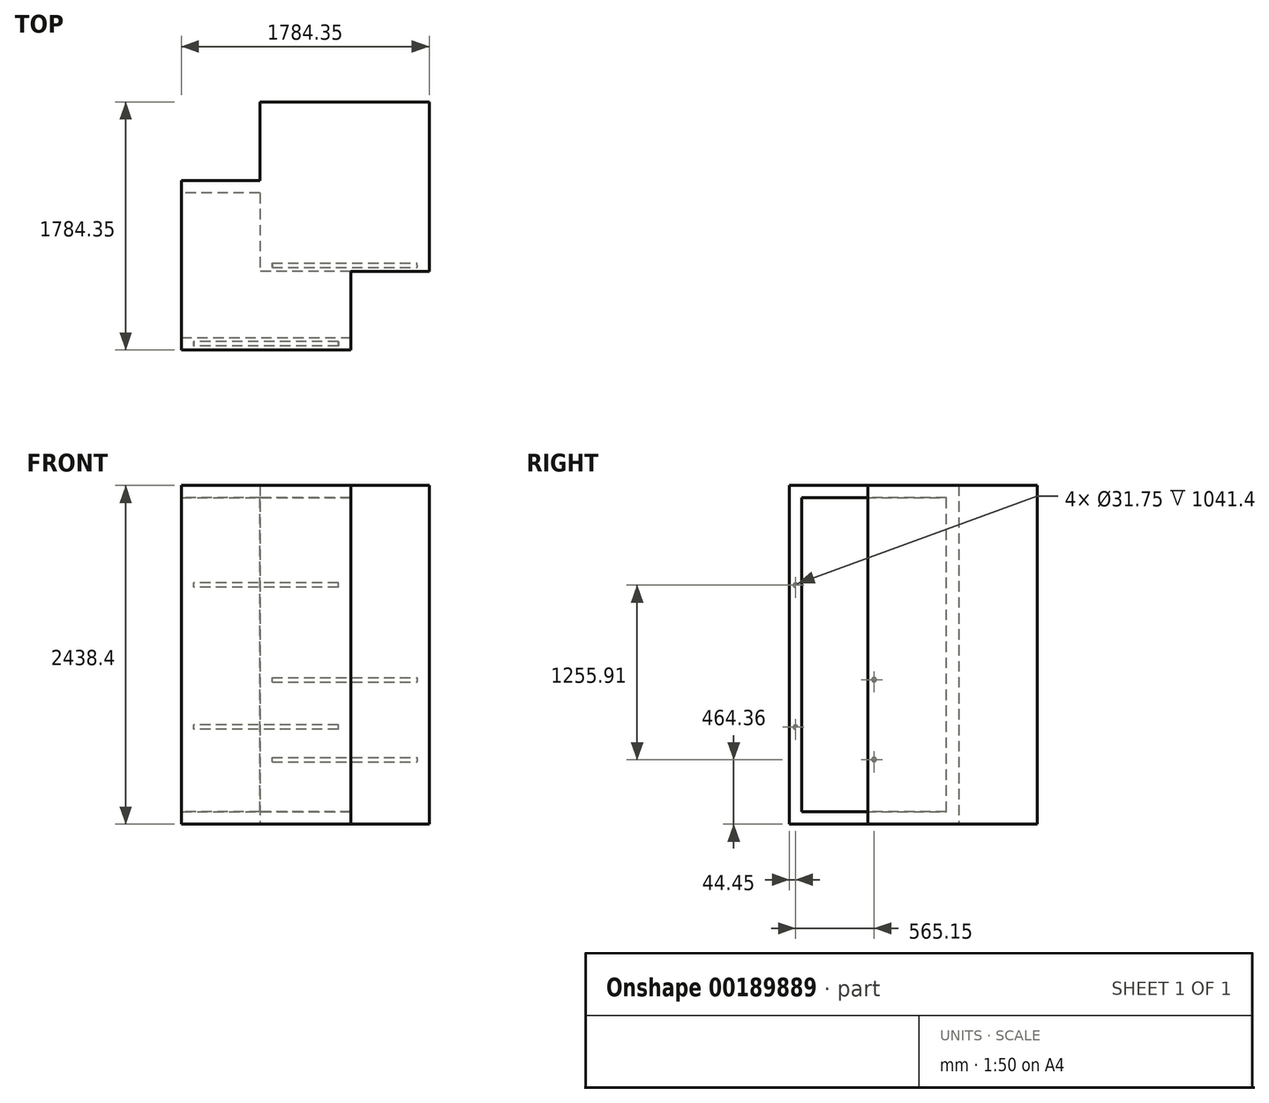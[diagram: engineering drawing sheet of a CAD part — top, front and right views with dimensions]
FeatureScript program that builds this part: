
annotation { "Feature Type Name" : "Feature", "Feature Type Description" : "" }
export const myFeature = defineFeature(function(context is Context, id is Id, definition is map)
    precondition{}
    {
        {
            var Q0;
            Q0=qCreatedBy(makeId("Top.planeOp"),FACE);
            var sketch = newSketch(context, id + "F0", { "sketchPlane" : qUnion([Q0])});
            skLineSegment(sketch, "E0.bottom", {"start": v(0, 0) * mm, "end": v(1219.2, 0) * mm});
            skLineSegment(sketch, "E0.top", {"start": v(0, 1219.2) * mm, "end": v(1219.2, 1219.2) * mm});
            skLineSegment(sketch, "E0.left", {"start": v(0, 0) * mm, "end": v(0, 1219.2) * mm});
            skLineSegment(sketch, "E0.right", {"start": v(1219.2, 0) * mm, "end": v(1219.2, 1219.2) * mm});
            skLineSegment(sketch, "E1.bottom", {"start": v(1784.35, 1784.35) * mm, "end": v(565.15, 1784.35) * mm});
            skLineSegment(sketch, "E1.top", {"start": v(1784.35, 565.15) * mm, "end": v(565.15, 565.15) * mm});
            skLineSegment(sketch, "E1.left", {"start": v(1784.35, 1784.35) * mm, "end": v(1784.35, 565.15) * mm});
            skLineSegment(sketch, "E1.right", {"start": v(565.15, 1784.35) * mm, "end": v(565.15, 565.15) * mm});
            skLineSegment(sketch, "E2.0", {"start": v(1695.45, 1695.45) * mm, "end": v(1695.45, 654.05) * mm});
            skLineSegment(sketch, "E2.1", {"start": v(1695.45, 1695.45) * mm, "end": v(654.05, 1695.45) * mm});
            skLineSegment(sketch, "E2.2", {"start": v(654.05, 1695.45) * mm, "end": v(654.05, 654.05) * mm});
            skLineSegment(sketch, "E2.3", {"start": v(1695.45, 654.05) * mm, "end": v(654.05, 654.05) * mm});
            skLineSegment(sketch, "E3.0", {"start": v(88.9, 1130.3) * mm, "end": v(1130.3, 1130.3) * mm});
            skLineSegment(sketch, "E3.1", {"start": v(88.9, 88.9) * mm, "end": v(88.9, 1130.3) * mm});
            skLineSegment(sketch, "E3.2", {"start": v(88.9, 88.9) * mm, "end": v(1130.3, 88.9) * mm});
            skLineSegment(sketch, "E3.3", {"start": v(1130.3, 88.9) * mm, "end": v(1130.3, 1130.3) * mm});
            skLineSegment(sketch, "E4", {"start": v(88.9, 765.31) * mm, "end": v(565.15, 765.31) * mm, "construction": true});
            skLineSegment(sketch, "E5", {"start": v(654.05, 765.31) * mm, "end": v(1130.3, 765.31) * mm, "construction": true});
            skLineSegment(sketch, "E6", {"start": v(800.66, 88.9) * mm, "end": v(800.66, 565.15) * mm, "construction": true});
            skLineSegment(sketch, "E7", {"start": v(800.66, 654.05) * mm, "end": v(800.66, 1130.3) * mm, "construction": true});
            skLineSegment(sketch, "E8.bottom", {"start": v(1695.45, 654.05) * mm, "end": v(1784.35, 654.05) * mm});
            skLineSegment(sketch, "E8.top", {"start": v(1695.45, 565.15) * mm, "end": v(1784.35, 565.15) * mm});
            skLineSegment(sketch, "E8.left", {"start": v(1695.45, 654.05) * mm, "end": v(1695.45, 565.15) * mm});
            skLineSegment(sketch, "E8.right", {"start": v(1784.35, 654.05) * mm, "end": v(1784.35, 565.15) * mm});
            skLineSegment(sketch, "E9.bottom", {"start": v(654.05, 654.05) * mm, "end": v(565.15, 654.05) * mm});
            skLineSegment(sketch, "E9.top", {"start": v(654.05, 565.15) * mm, "end": v(565.15, 565.15) * mm});
            skLineSegment(sketch, "E9.left", {"start": v(654.05, 654.05) * mm, "end": v(654.05, 565.15) * mm});
            skLineSegment(sketch, "E9.right", {"start": v(565.15, 654.05) * mm, "end": v(565.15, 565.15) * mm});
            skLineSegment(sketch, "E10.bottom", {"start": v(654.05, 1695.45) * mm, "end": v(565.15, 1695.45) * mm});
            skLineSegment(sketch, "E10.top", {"start": v(654.05, 1784.35) * mm, "end": v(565.15, 1784.35) * mm});
            skLineSegment(sketch, "E10.left", {"start": v(654.05, 1695.45) * mm, "end": v(654.05, 1784.35) * mm});
            skLineSegment(sketch, "E10.right", {"start": v(565.15, 1695.45) * mm, "end": v(565.15, 1784.35) * mm});
            skLineSegment(sketch, "E11.bottom", {"start": v(1695.45, 1695.45) * mm, "end": v(1784.35, 1695.45) * mm});
            skLineSegment(sketch, "E11.top", {"start": v(1695.45, 1784.35) * mm, "end": v(1784.35, 1784.35) * mm});
            skLineSegment(sketch, "E11.left", {"start": v(1695.45, 1695.45) * mm, "end": v(1695.45, 1784.35) * mm});
            skLineSegment(sketch, "E11.right", {"start": v(1784.35, 1695.45) * mm, "end": v(1784.35, 1784.35) * mm});
            skSolve(sketch);
        }
        {
            var Q0;
            {var subQ1=sQuery(id+"F0.wireOp",EDGE,"E0.right");var subQ6=sQuery(id+"F0.wireOp",EDGE,"E0.top");var subQ10=makeQuery(id+"F0.imprint","INTERSECT",VERTEX,{"derivedFrom":[subQ6,subQ1]});Q0=makeQuery(id+"F0.imprint","IMPRINT",FACE,{"disambiguationData":[TD([[makeQuery(id+"F0.imprint","IMPRINT",EDGE,{"disambiguationData":[TD([[subQ10,1.0]])],"derivedFrom":subQ6}),-1.0]])]});}
            var Q1;
            {var subQ0=sQuery(id+"F0.wireOp",EDGE,"E1.top");var subQ1=sQuery(id+"F0.wireOp",EDGE,"E0.right");var subQ2=makeQuery(id+"F0.imprint","INTERSECT",VERTEX,{"derivedFrom":[subQ1,subQ0]});Q1=makeQuery(id+"F0.imprint","IMPRINT",FACE,{"disambiguationData":[TD([[makeQuery(id+"F0.imprint","IMPRINT",EDGE,{"disambiguationData":[TD([[subQ2,-1.0]])],"derivedFrom":subQ1}),1.0]])]});}
            var Q2;
            {var subQ1=sQuery(id+"F0.wireOp",EDGE,"E0.bottom");Q2=makeQuery(id+"F0.imprint","IMPRINT",FACE,{"disambiguationData":[TD([[makeQuery(id+"F0.imprint","IMPRINT",EDGE,{"derivedFrom":subQ1}),1.0]])]});}
            var Q3;
            {var subQ0=sQuery(id+"F0.wireOp",EDGE,"E1.right");var subQ1=sQuery(id+"F0.wireOp",EDGE,"E0.top");var subQ2=makeQuery(id+"F0.imprint","INTERSECT",VERTEX,{"derivedFrom":[subQ1,subQ0]});Q3=makeQuery(id+"F0.imprint","IMPRINT",FACE,{"disambiguationData":[TD([[makeQuery(id+"F0.imprint","IMPRINT",EDGE,{"disambiguationData":[TD([[subQ2,-1.0]])],"derivedFrom":subQ1}),-1.0]])]});}
            extrude(context, id + "F1", {"entities" : qUnion([Q0, Q1, Q2, Q3]), "depth" : 88.9 * mm});
        }
        {
            var Q0;
            Q0=makeQuery(id+"F1.opExtrude","CAP_FACE",FACE,{"disambiguationData":[OSD([sQuery(id+"F0.wireOp",EDGE,"E0.bottom"),sQuery(id+"F0.wireOp",EDGE,"E0.top"),sQuery(id+"F0.wireOp",EDGE,"E0.left"),sQuery(id+"F0.wireOp",EDGE,"E0.right"),sQuery(id+"F0.wireOp",EDGE,"E3.0"),sQuery(id+"F0.wireOp",EDGE,"E3.1"),sQuery(id+"F0.wireOp",EDGE,"E3.2"),sQuery(id+"F0.wireOp",EDGE,"E3.3")])],"isStart":false});
            var sketch = newSketch(context, id + "F2", { "sketchPlane" : qUnion([Q0])});
            skLineSegment(sketch, "E12.bottom", {"start": v(88.9, 1130.3) * mm, "end": v(0, 1130.3) * mm});
            skLineSegment(sketch, "E12.top", {"start": v(88.9, 1219.2) * mm, "end": v(0, 1219.2) * mm});
            skLineSegment(sketch, "E12.left", {"start": v(88.9, 1130.3) * mm, "end": v(88.9, 1219.2) * mm});
            skLineSegment(sketch, "E12.right", {"start": v(0, 1130.3) * mm, "end": v(0, 1219.2) * mm});
            skLineSegment(sketch, "E13.bottom", {"start": v(1130.3, 1130.3) * mm, "end": v(1219.2, 1130.3) * mm});
            skLineSegment(sketch, "E13.top", {"start": v(1130.3, 1219.2) * mm, "end": v(1219.2, 1219.2) * mm});
            skLineSegment(sketch, "E13.left", {"start": v(1130.3, 1130.3) * mm, "end": v(1130.3, 1219.2) * mm});
            skLineSegment(sketch, "E13.right", {"start": v(1219.2, 1130.3) * mm, "end": v(1219.2, 1219.2) * mm});
            skLineSegment(sketch, "E14.bottom", {"start": v(1130.3, 88.9) * mm, "end": v(1219.2, 88.9) * mm});
            skLineSegment(sketch, "E14.top", {"start": v(1130.3, 0) * mm, "end": v(1219.2, 0) * mm});
            skLineSegment(sketch, "E14.left", {"start": v(1130.3, 88.9) * mm, "end": v(1130.3, 0) * mm});
            skLineSegment(sketch, "E14.right", {"start": v(1219.2, 88.9) * mm, "end": v(1219.2, 0) * mm});
            skLineSegment(sketch, "E15.bottom", {"start": v(88.9, 88.9) * mm, "end": v(0, 88.9) * mm});
            skLineSegment(sketch, "E15.top", {"start": v(88.9, 0) * mm, "end": v(0, 0) * mm});
            skLineSegment(sketch, "E15.left", {"start": v(88.9, 88.9) * mm, "end": v(88.9, 0) * mm});
            skLineSegment(sketch, "E15.right", {"start": v(0, 88.9) * mm, "end": v(0, 0) * mm});
            skSolve(sketch);
        }
        {
            var Q0;
            Q0=makeQuery(id+"F2.imprint","IMPRINT",FACE,{"disambiguationData":[TD([[makeQuery(id+"F2.imprint","IMPRINT",EDGE,{"derivedFrom":sQuery(id+"F2.wireOp",EDGE,"E12.bottom")}),-1.0]])]});
            var Q1;
            Q1=makeQuery(id+"F2.imprint","IMPRINT",FACE,{"disambiguationData":[TD([[makeQuery(id+"F2.imprint","IMPRINT",EDGE,{"derivedFrom":sQuery(id+"F2.wireOp",EDGE,"E13.bottom")}),1.0]])]});
            var Q2;
            Q2=makeQuery(id+"F2.imprint","IMPRINT",FACE,{"disambiguationData":[TD([[makeQuery(id+"F2.imprint","IMPRINT",EDGE,{"derivedFrom":sQuery(id+"F2.wireOp",EDGE,"E14.bottom")}),-1.0]])]});
            var Q3;
            Q3=makeQuery(id+"F2.imprint","IMPRINT",FACE,{"disambiguationData":[TD([[makeQuery(id+"F2.imprint","IMPRINT",EDGE,{"derivedFrom":sQuery(id+"F2.wireOp",EDGE,"E15.bottom")}),1.0]])]});
            extrude(context, id + "F3", {"entities" : qUnion([Q0, Q1, Q2, Q3]), "operationType" : NewBodyOperationType.ADD, "depth" : 2260.6 * mm});
        }
        {
            var Q0;
            Q0=makeQuery(id+"F3.opExtrude","CAP_FACE",FACE,{"disambiguationData":[OSD([sQuery(id+"F2.wireOp",EDGE,"E12.bottom"),sQuery(id+"F2.wireOp",EDGE,"E12.top"),sQuery(id+"F2.wireOp",EDGE,"E12.left"),sQuery(id+"F2.wireOp",EDGE,"E12.right")])],"isStart":false});
            var sketch = newSketch(context, id + "F4", { "sketchPlane" : qUnion([Q0])});
            skPoint(sketch, "E16.0", {"position": v(0, 1219.2) * mm});
            skPoint(sketch, "E17.0", {"position": v(1219.2, 1219.2) * mm});
            skPoint(sketch, "E18.0", {"position": v(1219.2, 0) * mm});
            skPoint(sketch, "E19.0", {"position": v(0, 0) * mm});
            skLineSegment(sketch, "E20.bottom", {"start": v(0, 1219.2) * mm, "end": v(1219.2, 1219.2) * mm});
            skLineSegment(sketch, "E20.top", {"start": v(0, 0) * mm, "end": v(1219.2, 0) * mm});
            skLineSegment(sketch, "E20.left", {"start": v(0, 1219.2) * mm, "end": v(0, 0) * mm});
            skLineSegment(sketch, "E20.right", {"start": v(1219.2, 1219.2) * mm, "end": v(1219.2, 0) * mm});
            skPoint(sketch, "E21.0", {"position": v(88.9, 1130.3) * mm});
            skPoint(sketch, "E22.0", {"position": v(1130.3, 1130.3) * mm});
            skPoint(sketch, "E23.0", {"position": v(1130.3, 88.9) * mm});
            skPoint(sketch, "E24.0", {"position": v(88.9, 88.9) * mm});
            skLineSegment(sketch, "E25.bottom", {"start": v(88.9, 1130.3) * mm, "end": v(1130.3, 1130.3) * mm});
            skLineSegment(sketch, "E25.top", {"start": v(88.9, 88.9) * mm, "end": v(1130.3, 88.9) * mm});
            skLineSegment(sketch, "E25.left", {"start": v(88.9, 1130.3) * mm, "end": v(88.9, 88.9) * mm});
            skLineSegment(sketch, "E25.right", {"start": v(1130.3, 1130.3) * mm, "end": v(1130.3, 88.9) * mm});
            skSolve(sketch);
        }
        {
            var Q0;
            {var subQ4=makeQuery(id+"F3.opExtrude","CAP_EDGE",EDGE,{"disambiguationData":[OSD([sQuery(id+"F2.wireOp",EDGE,"E12.bottom")])],"isStart":false});Q0=makeQuery(id+"F4.imprint","IMPRINT",FACE,{"disambiguationData":[TD([[makeQuery(id+"F4.imprint","IMPRINT",EDGE,{"derivedFrom":subQ4}),-1.0]])]});}
            var Q1;
            {var subQ3=sQuery(id+"F4.wireOp",EDGE,"E20.top");Q1=makeQuery(id+"F4.imprint","IMPRINT",FACE,{"disambiguationData":[TD([[makeQuery(id+"F4.imprint","IMPRINT",EDGE,{"derivedFrom":subQ3}),1.0]])]});}
            extrude(context, id + "F5", {"entities" : qUnion([Q0, Q1]), "operationType" : NewBodyOperationType.ADD, "depth" : 88.9 * mm});
        }
        {
            var Q0;
            {var subQ5=sQuery(id+"F0.wireOp",EDGE,"E8.left");Q0=makeQuery(id+"F0.imprint","IMPRINT",FACE,{"disambiguationData":[TD([[makeQuery(id+"F0.imprint","IMPRINT",EDGE,{"derivedFrom":subQ5}),-1.0]])]});}
            var Q1;
            {var subQ0=sQuery(id+"F0.wireOp",EDGE,"E9.left");Q1=makeQuery(id+"F0.imprint","IMPRINT",FACE,{"disambiguationData":[TD([[makeQuery(id+"F0.imprint","IMPRINT",EDGE,{"derivedFrom":subQ0}),1.0]])]});}
            var Q2;
            Q2=makeQuery(id+"F0.imprint","IMPRINT",FACE,{"disambiguationData":[TD([[makeQuery(id+"F0.imprint","IMPRINT",EDGE,{"derivedFrom":sQuery(id+"F0.wireOp",EDGE,"E1.left")}),-1.0]])]});
            var Q3;
            Q3=makeQuery(id+"F0.imprint","IMPRINT",FACE,{"disambiguationData":[TD([[makeQuery(id+"F0.imprint","IMPRINT",EDGE,{"derivedFrom":sQuery(id+"F0.wireOp",EDGE,"E1.bottom")}),1.0]])]});
            var Q4;
            {var subQ5=sQuery(id+"F0.wireOp",EDGE,"E10.bottom");Q4=makeQuery(id+"F0.imprint","IMPRINT",FACE,{"disambiguationData":[TD([[makeQuery(id+"F0.imprint","IMPRINT",EDGE,{"derivedFrom":subQ5}),1.0]])]});}
            var Q5;
            {var subQ0=sQuery(id+"F0.wireOp",EDGE,"E9.bottom");Q5=makeQuery(id+"F0.imprint","IMPRINT",FACE,{"disambiguationData":[TD([[makeQuery(id+"F0.imprint","IMPRINT",EDGE,{"derivedFrom":subQ0}),-1.0]])]});}
            var Q6;
            {var subQ0=sQuery(id+"F0.wireOp",EDGE,"E1.top");var subQ1=sQuery(id+"F0.wireOp",EDGE,"E0.right");var subQ2=makeQuery(id+"F0.imprint","INTERSECT",VERTEX,{"derivedFrom":[subQ1,subQ0]});Q6=makeQuery(id+"F0.imprint","IMPRINT",FACE,{"disambiguationData":[TD([[makeQuery(id+"F0.imprint","IMPRINT",EDGE,{"disambiguationData":[TD([[subQ2,-1.0]])],"derivedFrom":subQ1}),1.0]])]});}
            var Q7;
            {var subQ0=sQuery(id+"F0.wireOp",EDGE,"E1.right");var subQ1=sQuery(id+"F0.wireOp",EDGE,"E0.top");var subQ2=makeQuery(id+"F0.imprint","INTERSECT",VERTEX,{"derivedFrom":[subQ1,subQ0]});Q7=makeQuery(id+"F0.imprint","IMPRINT",FACE,{"disambiguationData":[TD([[makeQuery(id+"F0.imprint","IMPRINT",EDGE,{"disambiguationData":[TD([[subQ2,-1.0]])],"derivedFrom":subQ1}),-1.0]])]});}
            var Q8;
            Q8=makeQuery(id+"F0.imprint","IMPRINT",FACE,{"disambiguationData":[TD([[makeQuery(id+"F0.imprint","IMPRINT",EDGE,{"derivedFrom":sQuery(id+"F0.wireOp",EDGE,"E8.bottom")}),-1.0]])]});
            var Q9;
            Q9=makeQuery(id+"F0.imprint","IMPRINT",FACE,{"disambiguationData":[TD([[makeQuery(id+"F0.imprint","IMPRINT",EDGE,{"derivedFrom":sQuery(id+"F0.wireOp",EDGE,"E11.bottom")}),1.0]])]});
            var Q10;
            Q10=makeQuery(id+"F0.imprint","IMPRINT",FACE,{"disambiguationData":[TD([[makeQuery(id+"F0.imprint","IMPRINT",EDGE,{"derivedFrom":sQuery(id+"F0.wireOp",EDGE,"E10.bottom")}),-1.0]])]});
            var Q11;
            Q11=makeQuery(id+"F0.imprint","IMPRINT",FACE,{"disambiguationData":[TD([[makeQuery(id+"F0.imprint","IMPRINT",EDGE,{"derivedFrom":sQuery(id+"F0.wireOp",EDGE,"E9.bottom")}),1.0]])]});
            extrude(context, id + "F6", {"entities" : qUnion([Q0, Q1, Q2, Q3, Q4, Q5, Q6, Q7, Q8, Q9, Q10, Q11]), "operationType" : NewBodyOperationType.ADD, "depth" : 88.9 * mm});
        }
        {
            var Q0;
            Q0=makeQuery(id+"F0.imprint","IMPRINT",FACE,{"disambiguationData":[TD([[makeQuery(id+"F0.imprint","IMPRINT",EDGE,{"derivedFrom":sQuery(id+"F0.wireOp",EDGE,"E8.bottom")}),-1.0]])]});
            var Q1;
            Q1=makeQuery(id+"F0.imprint","IMPRINT",FACE,{"disambiguationData":[TD([[makeQuery(id+"F0.imprint","IMPRINT",EDGE,{"derivedFrom":sQuery(id+"F0.wireOp",EDGE,"E9.bottom")}),1.0]])]});
            var Q2;
            Q2=makeQuery(id+"F0.imprint","IMPRINT",FACE,{"disambiguationData":[TD([[makeQuery(id+"F0.imprint","IMPRINT",EDGE,{"derivedFrom":sQuery(id+"F0.wireOp",EDGE,"E10.bottom")}),-1.0]])]});
            var Q3;
            Q3=makeQuery(id+"F0.imprint","IMPRINT",FACE,{"disambiguationData":[TD([[makeQuery(id+"F0.imprint","IMPRINT",EDGE,{"derivedFrom":sQuery(id+"F0.wireOp",EDGE,"E11.bottom")}),1.0]])]});
            extrude(context, id + "F7", {"entities" : qUnion([Q0, Q1, Q2, Q3]), "operationType" : NewBodyOperationType.ADD, "depth" : 2438.4 * mm});
        }
        {
            var Q0;
            Q0=makeQuery(id+"F7.opExtrude","CAP_FACE",FACE,{"disambiguationData":[OSD([sQuery(id+"F0.wireOp",EDGE,"E9.bottom"),sQuery(id+"F0.wireOp",EDGE,"E9.top"),sQuery(id+"F0.wireOp",EDGE,"E9.left"),sQuery(id+"F0.wireOp",EDGE,"E9.right")])],"isStart":false});
            var sketch = newSketch(context, id + "F8", { "sketchPlane" : qUnion([Q0])});
            skPoint(sketch, "E26.0", {"position": v(565.15, 1784.35) * mm});
            skPoint(sketch, "E27.0", {"position": v(1784.35, 1784.35) * mm});
            skPoint(sketch, "E28.0", {"position": v(1784.35, 565.15) * mm});
            skPoint(sketch, "E29.0", {"position": v(565.15, 565.15) * mm});
            skPoint(sketch, "E30.0", {"position": v(654.05, 1695.45) * mm});
            skPoint(sketch, "E31.0", {"position": v(1695.45, 1695.45) * mm});
            skPoint(sketch, "E32.0", {"position": v(1695.45, 654.05) * mm});
            skPoint(sketch, "E33.0", {"position": v(654.05, 654.05) * mm});
            skLineSegment(sketch, "E34.bottom", {"start": v(565.15, 1784.35) * mm, "end": v(1784.35, 1784.35) * mm});
            skLineSegment(sketch, "E34.top", {"start": v(565.15, 565.15) * mm, "end": v(1784.35, 565.15) * mm});
            skLineSegment(sketch, "E34.left", {"start": v(565.15, 1784.35) * mm, "end": v(565.15, 565.15) * mm});
            skLineSegment(sketch, "E34.right", {"start": v(1784.35, 1784.35) * mm, "end": v(1784.35, 565.15) * mm});
            skLineSegment(sketch, "E35.bottom", {"start": v(654.05, 1695.45) * mm, "end": v(1695.45, 1695.45) * mm});
            skLineSegment(sketch, "E35.top", {"start": v(654.05, 654.05) * mm, "end": v(1695.45, 654.05) * mm});
            skLineSegment(sketch, "E35.left", {"start": v(654.05, 1695.45) * mm, "end": v(654.05, 654.05) * mm});
            skLineSegment(sketch, "E35.right", {"start": v(1695.45, 1695.45) * mm, "end": v(1695.45, 654.05) * mm});
            skSolve(sketch);
        }
        {
            var Q0;
            {var subQ3=sQuery(id+"F8.wireOp",EDGE,"E34.bottom");Q0=makeQuery(id+"F8.imprint","IMPRINT",FACE,{"disambiguationData":[TD([[makeQuery(id+"F8.imprint","IMPRINT",EDGE,{"derivedFrom":subQ3}),-1.0]])]});}
            var Q1;
            {var subQ4=makeQuery(id+"F7.opExtrude","CAP_EDGE",EDGE,{"disambiguationData":[OSD([sQuery(id+"F0.wireOp",EDGE,"E9.bottom")])],"isStart":false});Q1=makeQuery(id+"F8.imprint","IMPRINT",FACE,{"disambiguationData":[TD([[makeQuery(id+"F8.imprint","IMPRINT",EDGE,{"derivedFrom":subQ4}),1.0]])]});}
            extrude(context, id + "F9", {"entities" : qUnion([Q0, Q1]), "operationType" : NewBodyOperationType.ADD, "oppositeDirection" : true, "depth" : 88.9 * mm});
        }
        {
            var Q0;
            Q0=makeQuery(id+"F5.boolean.opBoolean","MERGE",FACE,{"derivedFrom":[makeQuery(id+"F3.boolean.opBoolean","MERGE",FACE,{"derivedFrom":[makeQuery(id+"F1.opExtrude","SWEPT_FACE",FACE,{"disambiguationData":[OSD([sQuery(id+"F0.wireOp",EDGE,"E0.left")])]}),makeQuery(id+"F3.opExtrude","SWEPT_FACE",FACE,{"disambiguationData":[OSD([sQuery(id+"F2.wireOp",EDGE,"E12.right")])]}),makeQuery(id+"F3.opExtrude","SWEPT_FACE",FACE,{"disambiguationData":[OSD([sQuery(id+"F2.wireOp",EDGE,"E15.right")])]})]}),makeQuery(id+"F5.opExtrude","SWEPT_FACE",FACE,{"disambiguationData":[OSD([sQuery(id+"F4.wireOp",EDGE,"E20.left")])]})]});
            var sketch = newSketch(context, id + "F10", { "sketchPlane" : qUnion([Q0])});
            skLineSegment(sketch, "E36", {"start": v(-1174.75, 2438.4) * mm, "end": v(-1174.75, 0) * mm, "construction": true});
            skLineSegment(sketch, "E37", {"start": v(-1130.3, 88.9) * mm, "end": v(-1174.75, 88.9) * mm, "construction": true});
            skLineSegment(sketch, "E38", {"start": v(-1174.75, 88.9) * mm, "end": v(-1219.2, 88.9) * mm, "construction": true});
            skCircle(sketch, "E39", {"center": v(-1174.75, 698.5) * mm, "radius": 15.88 * mm});
            skCircle(sketch, "E40", {"center": v(-1174.75, 1720.28) * mm, "radius": 15.88 * mm});
            skLineSegment(sketch, "E41", {"start": v(-609.6, 2349.5) * mm, "end": v(-609.6, 88.9) * mm, "construction": true});
            skCircle(sketch, "E42.MirrorC", {"center": v(-44.45, 1720.28) * mm, "radius": 15.88 * mm});
            skCircle(sketch, "E43.MirrorC", {"center": v(-44.45, 698.5) * mm, "radius": 15.88 * mm});
            skSolve(sketch);
        }
        {
            var Q0;
            Q0=makeQuery(id+"F10.imprint","IMPRINT",FACE,{"disambiguationData":[TD([[makeQuery(id+"F10.imprint","IMPRINT",EDGE,{"derivedFrom":sQuery(id+"F10.wireOp",EDGE,"E40")}),1.0]])]});
            var Q1;
            Q1=makeQuery(id+"F10.imprint","IMPRINT",FACE,{"disambiguationData":[TD([[makeQuery(id+"F10.imprint","IMPRINT",EDGE,{"derivedFrom":sQuery(id+"F10.wireOp",EDGE,"E39")}),1.0]])]});
            var Q2;
            Q2=makeQuery(id+"F10.imprint","IMPRINT",FACE,{"disambiguationData":[TD([[makeQuery(id+"F10.imprint","IMPRINT",EDGE,{"derivedFrom":sQuery(id+"F10.wireOp",EDGE,"E42.MirrorC")}),-1.0]])]});
            var Q3;
            Q3=makeQuery(id+"F10.imprint","IMPRINT",FACE,{"disambiguationData":[TD([[makeQuery(id+"F10.imprint","IMPRINT",EDGE,{"derivedFrom":sQuery(id+"F10.wireOp",EDGE,"E43.MirrorC")}),-1.0]])]});
            var Q4;
            {var subQ4=sQuery(id+"F4.wireOp",EDGE,"E20.right");var subQ36=sQuery(id+"F0.wireOp",EDGE,"E0.right");var subQ38=sQuery(id+"F0.wireOp",EDGE,"E0.top");Q4=makeQuery(id+"F9.boolean.opBoolean","SPLIT",FACE,{"disambiguationData":[TD([makeQuery(id+"F1.opExtrude","SWEPT_FACE",FACE,{"disambiguationData":[OSD([subQ38])]})])],"derivedFrom":makeQuery(id+"F5.boolean.opBoolean","MERGE",FACE,{"derivedFrom":[makeQuery(id+"F3.boolean.opBoolean","MERGE",FACE,{"derivedFrom":[makeQuery(id+"F1.opExtrude","SWEPT_FACE",FACE,{"disambiguationData":[OSD([subQ36])]}),makeQuery(id+"F3.opExtrude","SWEPT_FACE",FACE,{"disambiguationData":[OSD([sQuery(id+"F2.wireOp",EDGE,"E13.right")])]}),makeQuery(id+"F3.opExtrude","SWEPT_FACE",FACE,{"disambiguationData":[OSD([sQuery(id+"F2.wireOp",EDGE,"E14.right")])]})]}),makeQuery(id+"F5.opExtrude","SWEPT_FACE",FACE,{"disambiguationData":[OSD([subQ4])]})]})});}
            extrude(context, id + "F11", {"entities" : qUnion([Q0, Q1, Q2, Q3]), "operationType" : NewBodyOperationType.ADD, "endBound" : BoundingType.UP_TO_SURFACE, "oppositeDirection" : true, "endBoundEntityFace" : qUnion([Q4]), "depth" : 25.4 * mm});
        }
        {
            var Q0;
            {var subQ0=sQuery(id+"F0.wireOp",EDGE,"E11.top");var subQ1=sQuery(id+"F0.wireOp",EDGE,"E10.top");Q0=makeQuery(id+"F9.boolean.opBoolean","MERGE",FACE,{"derivedFrom":[makeQuery(id+"F7.boolean.opBoolean","MERGE",FACE,{"derivedFrom":[makeQuery(id+"F6.opExtrude","SWEPT_FACE",FACE,{"disambiguationData":[OSD([sQuery(id+"F0.wireOp",EDGE,"E1.bottom"),subQ1,subQ0])]}),makeQuery(id+"F7.opExtrude","SWEPT_FACE",FACE,{"disambiguationData":[OSD([subQ1])]}),makeQuery(id+"F7.opExtrude","SWEPT_FACE",FACE,{"disambiguationData":[OSD([subQ0])]})]}),makeQuery(id+"F9.opExtrude","SWEPT_FACE",FACE,{"disambiguationData":[OSD([sQuery(id+"F8.wireOp",EDGE,"E34.bottom")])]})]});}
            var sketch = newSketch(context, id + "F12", { "sketchPlane" : qUnion([Q0])});
            skLineSegment(sketch, "E44", {"start": v(-609.6, 2438.4) * mm, "end": v(-609.6, 0) * mm, "construction": true});
            skLineSegment(sketch, "E45", {"start": v(-654.05, 88.9) * mm, "end": v(-609.6, 88.9) * mm, "construction": true});
            skLineSegment(sketch, "E46", {"start": v(-609.6, 88.9) * mm, "end": v(-565.15, 88.9) * mm, "construction": true});
            skCircle(sketch, "E47", {"center": v(-609.6, 1269.17) * mm, "radius": 15.88 * mm});
            skCircle(sketch, "E48", {"center": v(-609.6, 2098.03) * mm, "radius": 15.88 * mm});
            skLineSegment(sketch, "E49", {"start": v(-1174.75, 2349.5) * mm, "end": v(-1174.75, 88.9) * mm, "construction": true});
            skCircle(sketch, "E50.MirrorC", {"center": v(-1739.9, 2098.03) * mm, "radius": 15.88 * mm});
            skCircle(sketch, "E51.MirrorC", {"center": v(-1739.9, 1269.17) * mm, "radius": 15.88 * mm});
            skSolve(sketch);
        }
        {
            var Q0;
            Q0=makeQuery(id+"F12.imprint","IMPRINT",FACE,{"disambiguationData":[TD([[makeQuery(id+"F12.imprint","IMPRINT",EDGE,{"derivedFrom":sQuery(id+"F12.wireOp",EDGE,"E48")}),1.0]])]});
            var Q1;
            Q1=makeQuery(id+"F12.imprint","IMPRINT",FACE,{"disambiguationData":[TD([[makeQuery(id+"F12.imprint","IMPRINT",EDGE,{"derivedFrom":sQuery(id+"F12.wireOp",EDGE,"E47")}),1.0]])]});
            var Q2;
            Q2=makeQuery(id+"F12.imprint","IMPRINT",FACE,{"disambiguationData":[TD([[makeQuery(id+"F12.imprint","IMPRINT",EDGE,{"derivedFrom":sQuery(id+"F12.wireOp",EDGE,"E50.MirrorC")}),-1.0]])]});
            var Q3;
            Q3=makeQuery(id+"F12.imprint","IMPRINT",FACE,{"disambiguationData":[TD([[makeQuery(id+"F12.imprint","IMPRINT",EDGE,{"derivedFrom":sQuery(id+"F12.wireOp",EDGE,"E51.MirrorC")}),-1.0]])]});
            var Q4;
            {var subQ0=sQuery(id+"F0.wireOp",EDGE,"E9.top");var subQ7=sQuery(id+"F0.wireOp",EDGE,"E8.top");var subQ14=sQuery(id+"F0.wireOp",EDGE,"E1.top");var subQ16=sQuery(id+"F0.wireOp",EDGE,"E3.3");Q4=makeQuery(id+"F9.boolean.opBoolean","MERGE",FACE,{"derivedFrom":[makeQuery(id+"F7.boolean.opBoolean","MERGE",FACE,{"derivedFrom":[makeQuery(id+"F6.boolean.opBoolean","SPLIT",FACE,{"disambiguationData":[TD([makeQuery(id+"F1.opExtrude","SWEPT_FACE",FACE,{"disambiguationData":[OSD([subQ16])]})])],"derivedFrom":makeQuery(id+"F6.opExtrude","SWEPT_FACE",FACE,{"disambiguationData":[OSD([subQ14,subQ7,subQ0])]})}),makeQuery(id+"F7.opExtrude","SWEPT_FACE",FACE,{"disambiguationData":[OSD([subQ0])]})]}),makeQuery(id+"F9.opExtrude","SWEPT_FACE",FACE,{"disambiguationData":[OSD([sQuery(id+"F8.wireOp",EDGE,"E34.top")])]})]});}
            extrude(context, id + "F13", {"entities" : qUnion([Q0, Q1, Q2, Q3]), "operationType" : NewBodyOperationType.ADD, "endBound" : BoundingType.UP_TO_SURFACE, "oppositeDirection" : true, "endBoundEntityFace" : qUnion([Q4]), "depth" : 25.4 * mm});
        }
        {
            var Q0;
            {var subQ0=sQuery(id+"F0.wireOp",EDGE,"E11.right");var subQ1=sQuery(id+"F0.wireOp",EDGE,"E8.right");Q0=makeQuery(id+"F9.boolean.opBoolean","MERGE",FACE,{"derivedFrom":[makeQuery(id+"F7.boolean.opBoolean","MERGE",FACE,{"derivedFrom":[makeQuery(id+"F6.opExtrude","SWEPT_FACE",FACE,{"disambiguationData":[OSD([sQuery(id+"F0.wireOp",EDGE,"E1.left"),subQ1,subQ0])]}),makeQuery(id+"F7.opExtrude","SWEPT_FACE",FACE,{"disambiguationData":[OSD([subQ1])]}),makeQuery(id+"F7.opExtrude","SWEPT_FACE",FACE,{"disambiguationData":[OSD([subQ0])]})]}),makeQuery(id+"F9.opExtrude","SWEPT_FACE",FACE,{"disambiguationData":[OSD([sQuery(id+"F8.wireOp",EDGE,"E34.right")])]})]});}
            var sketch = newSketch(context, id + "F14", { "sketchPlane" : qUnion([Q0])});
            skLineSegment(sketch, "E52", {"start": v(1739.9, 2438.4) * mm, "end": v(1739.9, 0) * mm, "construction": true});
            skLineSegment(sketch, "E53", {"start": v(1695.45, 88.9) * mm, "end": v(1739.9, 88.9) * mm, "construction": true});
            skLineSegment(sketch, "E54", {"start": v(1739.9, 88.9) * mm, "end": v(1784.35, 88.9) * mm, "construction": true});
            skCircle(sketch, "E55", {"center": v(1739.9, 1039.7) * mm, "radius": 15.88 * mm});
            skCircle(sketch, "E56", {"center": v(1739.9, 464.36) * mm, "radius": 15.88 * mm});
            skLineSegment(sketch, "E57", {"start": v(1174.75, 2349.5) * mm, "end": v(1174.75, 88.9) * mm, "construction": true});
            skCircle(sketch, "E58.MirrorC", {"center": v(609.6, 1039.7) * mm, "radius": 15.88 * mm});
            skCircle(sketch, "E59.MirrorC", {"center": v(609.6, 464.36) * mm, "radius": 15.88 * mm});
            skSolve(sketch);
        }
        {
            var Q0;
            Q0=makeQuery(id+"F14.imprint","IMPRINT",FACE,{"disambiguationData":[TD([[makeQuery(id+"F14.imprint","IMPRINT",EDGE,{"derivedFrom":sQuery(id+"F14.wireOp",EDGE,"E58.MirrorC")}),-1.0]])]});
            var Q1;
            Q1=makeQuery(id+"F14.imprint","IMPRINT",FACE,{"disambiguationData":[TD([[makeQuery(id+"F14.imprint","IMPRINT",EDGE,{"derivedFrom":sQuery(id+"F14.wireOp",EDGE,"E55")}),1.0]])]});
            var Q2;
            Q2=makeQuery(id+"F14.imprint","IMPRINT",FACE,{"disambiguationData":[TD([[makeQuery(id+"F14.imprint","IMPRINT",EDGE,{"derivedFrom":sQuery(id+"F14.wireOp",EDGE,"E56")}),1.0]])]});
            var Q3;
            Q3=makeQuery(id+"F14.imprint","IMPRINT",FACE,{"disambiguationData":[TD([[makeQuery(id+"F14.imprint","IMPRINT",EDGE,{"derivedFrom":sQuery(id+"F14.wireOp",EDGE,"E59.MirrorC")}),-1.0]])]});
            var Q4;
            {var subQ0=sQuery(id+"F0.wireOp",EDGE,"E9.right");var subQ3=sQuery(id+"F0.wireOp",EDGE,"E10.right");var subQ12=sQuery(id+"F0.wireOp",EDGE,"E1.right");var subQ16=sQuery(id+"F0.wireOp",EDGE,"E3.0");Q4=makeQuery(id+"F9.boolean.opBoolean","MERGE",FACE,{"derivedFrom":[makeQuery(id+"F7.boolean.opBoolean","MERGE",FACE,{"derivedFrom":[makeQuery(id+"F6.boolean.opBoolean","SPLIT",FACE,{"disambiguationData":[TD([makeQuery(id+"F1.opExtrude","SWEPT_FACE",FACE,{"disambiguationData":[OSD([subQ16])]})])],"derivedFrom":makeQuery(id+"F6.opExtrude","SWEPT_FACE",FACE,{"disambiguationData":[OSD([subQ12,subQ0,subQ3])]})}),makeQuery(id+"F7.opExtrude","SWEPT_FACE",FACE,{"disambiguationData":[OSD([subQ0])]})]}),makeQuery(id+"F9.opExtrude","SWEPT_FACE",FACE,{"disambiguationData":[OSD([sQuery(id+"F8.wireOp",EDGE,"E34.left")])]})]});}
            extrude(context, id + "F15", {"entities" : qUnion([Q0, Q1, Q2, Q3]), "operationType" : NewBodyOperationType.ADD, "endBound" : BoundingType.UP_TO_SURFACE, "oppositeDirection" : true, "endBoundEntityFace" : qUnion([Q4]), "depth" : 25.4 * mm});
        }
        {
            var Q0;
            Q0=makeQuery(id+"F5.boolean.opBoolean","MERGE",FACE,{"derivedFrom":[makeQuery(id+"F3.boolean.opBoolean","MERGE",FACE,{"derivedFrom":[makeQuery(id+"F1.opExtrude","SWEPT_FACE",FACE,{"disambiguationData":[OSD([sQuery(id+"F0.wireOp",EDGE,"E0.bottom")])]}),makeQuery(id+"F3.opExtrude","SWEPT_FACE",FACE,{"disambiguationData":[OSD([sQuery(id+"F2.wireOp",EDGE,"E14.top")])]}),makeQuery(id+"F3.opExtrude","SWEPT_FACE",FACE,{"disambiguationData":[OSD([sQuery(id+"F2.wireOp",EDGE,"E15.top")])]})]}),makeQuery(id+"F5.opExtrude","SWEPT_FACE",FACE,{"disambiguationData":[OSD([sQuery(id+"F4.wireOp",EDGE,"E20.top")])]})]});
            var sketch = newSketch(context, id + "F16", { "sketchPlane" : qUnion([Q0])});
            skLineSegment(sketch, "E60", {"start": v(1130.3, 1990.29) * mm, "end": v(771.09, 2349.5) * mm});
            skLineSegment(sketch, "E61", {"start": v(771.09, 2349.5) * mm, "end": v(896.81, 2349.5) * mm});
            skLineSegment(sketch, "E62", {"start": v(896.81, 2349.5) * mm, "end": v(1130.3, 2116.01) * mm});
            skLineSegment(sketch, "E63", {"start": v(1130.3, 2116.01) * mm, "end": v(1130.3, 1990.29) * mm});
            skLineSegment(sketch, "E64", {"start": v(609.6, 2349.5) * mm, "end": v(609.6, 88.9) * mm, "construction": true});
            skLineSegment(sketch, "E65", {"start": v(1130.3, 1219.2) * mm, "end": v(88.9, 1219.2) * mm, "construction": true});
            skLineSegment(sketch, "E66.MirrorCS", {"start": v(88.9, 1990.29) * mm, "end": v(448.11, 2349.5) * mm});
            skLineSegment(sketch, "E67.MirrorCS", {"start": v(322.39, 2349.5) * mm, "end": v(88.9, 2116.01) * mm});
            skLineSegment(sketch, "E68.MirrorCS", {"start": v(448.11, 2349.5) * mm, "end": v(322.39, 2349.5) * mm});
            skLineSegment(sketch, "E69.MirrorCS", {"start": v(88.9, 2116.01) * mm, "end": v(88.9, 1990.29) * mm});
            skLineSegment(sketch, "E70.MirrorCS", {"start": v(1130.3, 448.11) * mm, "end": v(771.09, 88.9) * mm});
            skLineSegment(sketch, "E71.MirrorCS", {"start": v(896.81, 88.9) * mm, "end": v(1130.3, 322.39) * mm});
            skLineSegment(sketch, "E72.MirrorCS", {"start": v(771.09, 88.9) * mm, "end": v(896.81, 88.9) * mm});
            skLineSegment(sketch, "E73.MirrorCS", {"start": v(1130.3, 322.39) * mm, "end": v(1130.3, 448.11) * mm});
            skLineSegment(sketch, "E74.MirrorCS", {"start": v(88.9, 448.11) * mm, "end": v(448.11, 88.9) * mm});
            skLineSegment(sketch, "E75.MirrorCS", {"start": v(322.39, 88.9) * mm, "end": v(88.9, 322.39) * mm});
            skLineSegment(sketch, "E76.MirrorCS", {"start": v(448.11, 88.9) * mm, "end": v(322.39, 88.9) * mm});
            skLineSegment(sketch, "E77.MirrorCS", {"start": v(88.9, 322.39) * mm, "end": v(88.9, 448.11) * mm});
            skSolve(sketch);
        }
        {
            var Q0;
            Q0=makeQuery(id+"F16.imprint","IMPRINT",FACE,{"disambiguationData":[TD([[makeQuery(id+"F16.imprint","IMPRINT",EDGE,{"derivedFrom":sQuery(id+"F16.wireOp",EDGE,"E66.MirrorCS")}),1.0]])]});
            var Q1;
            Q1=makeQuery(id+"F16.imprint","IMPRINT",FACE,{"disambiguationData":[TD([[makeQuery(id+"F16.imprint","IMPRINT",EDGE,{"derivedFrom":sQuery(id+"F16.wireOp",EDGE,"E60")}),-1.0]])]});
            var Q2;
            Q2=makeQuery(id+"F16.imprint","IMPRINT",FACE,{"disambiguationData":[TD([[makeQuery(id+"F16.imprint","IMPRINT",EDGE,{"derivedFrom":sQuery(id+"F16.wireOp",EDGE,"E70.MirrorCS")}),1.0]])]});
            var Q3;
            Q3=makeQuery(id+"F16.imprint","IMPRINT",FACE,{"disambiguationData":[TD([[makeQuery(id+"F16.imprint","IMPRINT",EDGE,{"derivedFrom":sQuery(id+"F16.wireOp",EDGE,"E74.MirrorCS")}),-1.0]])]});
            var Q4;
            Q4=makeQuery(id+"F3.opExtrude","SWEPT_FACE",FACE,{"disambiguationData":[OSD([sQuery(id+"F2.wireOp",EDGE,"E15.bottom")])]});
            extrude(context, id + "F17", {"entities" : qUnion([Q0, Q1, Q2, Q3]), "operationType" : NewBodyOperationType.ADD, "endBound" : BoundingType.UP_TO_SURFACE, "oppositeDirection" : true, "endBoundEntityFace" : qUnion([Q4]), "depth" : 25.4 * mm});
        }
        {
            var Q0;
            Q0=makeQuery(id+"F9.boolean.opBoolean","MERGE",FACE,{"derivedFrom":[makeQuery(id+"F5.opExtrude","CAP_FACE",FACE,{"disambiguationData":[OSD([sQuery(id+"F4.wireOp",EDGE,"E20.bottom"),sQuery(id+"F4.wireOp",EDGE,"E20.top"),sQuery(id+"F4.wireOp",EDGE,"E20.left"),sQuery(id+"F4.wireOp",EDGE,"E20.right"),sQuery(id+"F4.wireOp",EDGE,"E25.bottom"),sQuery(id+"F4.wireOp",EDGE,"E25.top"),sQuery(id+"F4.wireOp",EDGE,"E25.left"),sQuery(id+"F4.wireOp",EDGE,"E25.right")])],"isStart":false}),makeQuery(id+"F7.opExtrude","CAP_FACE",FACE,{"disambiguationData":[OSD([sQuery(id+"F0.wireOp",EDGE,"E8.bottom"),sQuery(id+"F0.wireOp",EDGE,"E8.top"),sQuery(id+"F0.wireOp",EDGE,"E8.left"),sQuery(id+"F0.wireOp",EDGE,"E8.right")])],"isStart":false}),makeQuery(id+"F7.opExtrude","CAP_FACE",FACE,{"disambiguationData":[OSD([sQuery(id+"F0.wireOp",EDGE,"E9.bottom"),sQuery(id+"F0.wireOp",EDGE,"E9.top"),sQuery(id+"F0.wireOp",EDGE,"E9.left"),sQuery(id+"F0.wireOp",EDGE,"E9.right")])],"isStart":false}),makeQuery(id+"F7.opExtrude","CAP_FACE",FACE,{"disambiguationData":[OSD([sQuery(id+"F0.wireOp",EDGE,"E10.bottom"),sQuery(id+"F0.wireOp",EDGE,"E10.top"),sQuery(id+"F0.wireOp",EDGE,"E10.left"),sQuery(id+"F0.wireOp",EDGE,"E10.right")])],"isStart":false}),makeQuery(id+"F7.opExtrude","CAP_FACE",FACE,{"disambiguationData":[OSD([sQuery(id+"F0.wireOp",EDGE,"E11.bottom"),sQuery(id+"F0.wireOp",EDGE,"E11.top"),sQuery(id+"F0.wireOp",EDGE,"E11.left"),sQuery(id+"F0.wireOp",EDGE,"E11.right")])],"isStart":false}),makeQuery(id+"F9.opExtrude","CAP_FACE",FACE,{"disambiguationData":[OSD([sQuery(id+"F8.wireOp",EDGE,"E34.bottom"),sQuery(id+"F8.wireOp",EDGE,"E34.top"),sQuery(id+"F8.wireOp",EDGE,"E34.left"),sQuery(id+"F8.wireOp",EDGE,"E34.right"),sQuery(id+"F8.wireOp",EDGE,"E35.bottom"),sQuery(id+"F8.wireOp",EDGE,"E35.top"),sQuery(id+"F8.wireOp",EDGE,"E35.left"),sQuery(id+"F8.wireOp",EDGE,"E35.right")])],"isStart":true})]});
            var sketch = newSketch(context, id + "F18", { "sketchPlane" : qUnion([Q0])});
            skLineSegment(sketch, "E78.bottom", {"start": v(654.05, 1695.45) * mm, "end": v(1695.45, 1695.45) * mm, "construction": true});
            skLineSegment(sketch, "E78.top", {"start": v(654.05, 654.05) * mm, "end": v(1695.45, 654.05) * mm, "construction": true});
            skLineSegment(sketch, "E78.left", {"start": v(654.05, 1695.45) * mm, "end": v(654.05, 654.05) * mm, "construction": true});
            skLineSegment(sketch, "E78.right", {"start": v(1695.45, 1695.45) * mm, "end": v(1695.45, 654.05) * mm, "construction": true});
            skLineSegment(sketch, "E79.bottom", {"start": v(1130.3, 1130.3) * mm, "end": v(88.9, 1130.3) * mm, "construction": true});
            skLineSegment(sketch, "E79.top", {"start": v(1130.3, 88.9) * mm, "end": v(88.9, 88.9) * mm, "construction": true});
            skLineSegment(sketch, "E79.left", {"start": v(1130.3, 1130.3) * mm, "end": v(1130.3, 88.9) * mm, "construction": true});
            skLineSegment(sketch, "E79.right", {"start": v(88.9, 1130.3) * mm, "end": v(88.9, 88.9) * mm, "construction": true});
            skLineSegment(sketch, "E80", {"start": v(654.05, 1461.96) * mm, "end": v(887.54, 1695.45) * mm});
            skLineSegment(sketch, "E81", {"start": v(887.54, 1695.45) * mm, "end": v(1013.26, 1695.45) * mm});
            skLineSegment(sketch, "E82", {"start": v(1013.26, 1695.45) * mm, "end": v(654.05, 1336.24) * mm});
            skLineSegment(sketch, "E83", {"start": v(654.05, 1336.24) * mm, "end": v(654.05, 1461.96) * mm});
            skLineSegment(sketch, "E84", {"start": v(654.05, 1174.75) * mm, "end": v(1695.45, 1174.75) * mm, "construction": true});
            skLineSegment(sketch, "E85.MirrorCS", {"start": v(1013.26, 654.05) * mm, "end": v(654.05, 1013.26) * mm});
            skLineSegment(sketch, "E86.MirrorCS", {"start": v(654.05, 887.54) * mm, "end": v(887.54, 654.05) * mm});
            skLineSegment(sketch, "E87", {"start": v(1174.75, 1695.45) * mm, "end": v(1174.75, 654.05) * mm, "construction": true});
            skLineSegment(sketch, "E88.MirrorCS", {"start": v(1336.24, 1695.45) * mm, "end": v(1695.45, 1336.24) * mm});
            skLineSegment(sketch, "E89.MirrorCS", {"start": v(1695.45, 1461.96) * mm, "end": v(1461.96, 1695.45) * mm});
            skLineSegment(sketch, "E90.MirrorCS", {"start": v(1336.24, 654.05) * mm, "end": v(1695.45, 1013.26) * mm});
            skLineSegment(sketch, "E91.MirrorCS", {"start": v(1695.45, 887.54) * mm, "end": v(1461.96, 654.05) * mm});
            skSolve(sketch);
        }
        {
            var Q0;
            Q0=makeQuery(id+"F18.imprint","IMPRINT",FACE,{"disambiguationData":[TD([[makeQuery(id+"F18.imprint","IMPRINT",EDGE,{"derivedFrom":sQuery(id+"F18.wireOp",EDGE,"E80")}),-1.0]])]});
            var Q1;
            {var subQ0=sQuery(id+"F18.wireOp",EDGE,"E88.MirrorCS");Q1=makeQuery(id+"F18.imprint","IMPRINT",FACE,{"disambiguationData":[TD([[makeQuery(id+"F18.imprint","IMPRINT",EDGE,{"derivedFrom":subQ0}),1.0]])]});}
            var Q2;
            {var subQ0=sQuery(id+"F18.wireOp",EDGE,"E90.MirrorCS");Q2=makeQuery(id+"F18.imprint","IMPRINT",FACE,{"disambiguationData":[TD([[makeQuery(id+"F18.imprint","IMPRINT",EDGE,{"derivedFrom":subQ0}),-1.0]])]});}
            var Q3;
            {var subQ0=sQuery(id+"F18.wireOp",EDGE,"E85.MirrorCS");Q3=makeQuery(id+"F18.imprint","IMPRINT",FACE,{"disambiguationData":[TD([[makeQuery(id+"F18.imprint","IMPRINT",EDGE,{"derivedFrom":subQ0}),1.0]])]});}
            var Q4;
            {var subQ0=sQuery(id+"F8.wireOp",EDGE,"E35.right");var subQ1=sQuery(id+"F8.wireOp",EDGE,"E35.top");var subQ2=sQuery(id+"F8.wireOp",EDGE,"E35.bottom");var subQ3=sQuery(id+"F8.wireOp",EDGE,"E34.right");var subQ4=makeQuery(id+"F9.opExtrude","CAP_FACE",FACE,{"disambiguationData":[OSD([sQuery(id+"F8.wireOp",EDGE,"E34.bottom"),sQuery(id+"F8.wireOp",EDGE,"E34.top"),sQuery(id+"F8.wireOp",EDGE,"E34.left"),subQ3,subQ2,subQ1,sQuery(id+"F8.wireOp",EDGE,"E35.left"),subQ0])],"isStart":false});Q4=makeQuery(id+"F9.boolean.opBoolean","SPLIT",FACE,{"disambiguationData":[TD([makeQuery(id+"F7.opExtrude","SWEPT_FACE",FACE,{"disambiguationData":[OSD([sQuery(id+"F0.wireOp",EDGE,"E8.bottom")])]})])],"derivedFrom":subQ4});}
            var Q5;
            {var subQ0=sQuery(id+"F8.wireOp",EDGE,"E35.right");var subQ1=sQuery(id+"F8.wireOp",EDGE,"E35.top");var subQ2=sQuery(id+"F8.wireOp",EDGE,"E35.bottom");var subQ3=sQuery(id+"F8.wireOp",EDGE,"E34.right");var subQ4=makeQuery(id+"F9.opExtrude","CAP_FACE",FACE,{"disambiguationData":[OSD([sQuery(id+"F8.wireOp",EDGE,"E34.bottom"),sQuery(id+"F8.wireOp",EDGE,"E34.top"),sQuery(id+"F8.wireOp",EDGE,"E34.left"),subQ3,subQ2,subQ1,sQuery(id+"F8.wireOp",EDGE,"E35.left"),subQ0])],"isStart":false});Q5=makeQuery(id+"F9.boolean.opBoolean","SPLIT",FACE,{"disambiguationData":[TD([makeQuery(id+"F7.opExtrude","SWEPT_FACE",FACE,{"disambiguationData":[OSD([sQuery(id+"F0.wireOp",EDGE,"E8.bottom")])]})])],"derivedFrom":subQ4});}
            extrude(context, id + "F19", {"entities" : qUnion([Q0, Q1, Q2, Q3, Q4]), "operationType" : NewBodyOperationType.ADD, "oppositeDirection" : true, "endBoundEntityFace" : qUnion([Q5]), "depth" : 88.9 * mm});
        }
    });
